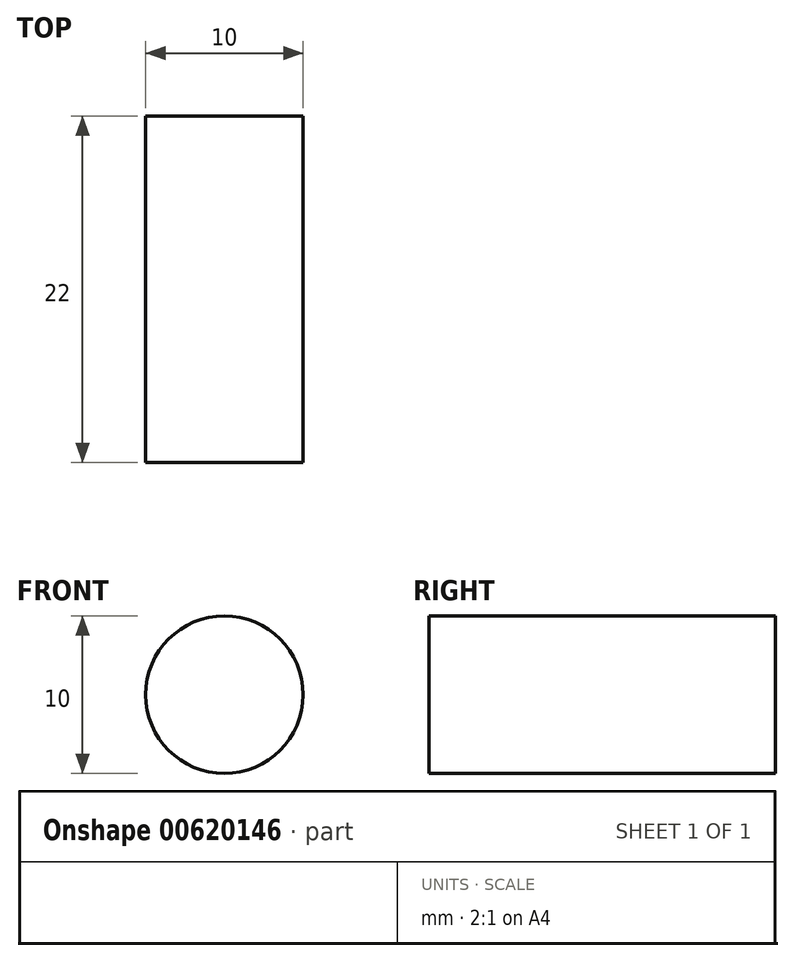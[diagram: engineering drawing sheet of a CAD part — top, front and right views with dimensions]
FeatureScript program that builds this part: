
annotation { "Feature Type Name" : "Feature", "Feature Type Description" : "" }
export const myFeature = defineFeature(function(context is Context, id is Id, definition is map)
    precondition{}
    {
        {
            var Q0;
            Q0=qCreatedBy(makeId("Front.planeOp"),FACE);
            var sketch = newSketch(context, id + "F0", { "sketchPlane" : qUnion([Q0])});
            skCircle(sketch, "E0", {"center": v(0, 0) * mm, "radius": 5 * mm});
            skSolve(sketch);
        }
        {
            var Q0;
            Q0=makeQuery(id+"F0.imprint","IMPRINT",FACE,{"disambiguationData":[TD([[makeQuery(id+"F0.imprint","IMPRINT",EDGE,{"derivedFrom":sQuery(id+"F0.wireOp",EDGE,"E0")}),1.0]])]});
            extrude(context, id + "F1", {"entities" : qUnion([Q0]), "oppositeDirection" : true, "depth" : 22 * mm, "offsetDistance" : 25 * mm, "symmetric" : true});
        }
    });
